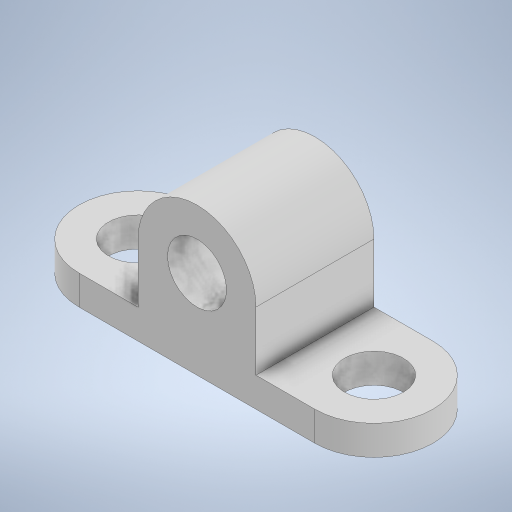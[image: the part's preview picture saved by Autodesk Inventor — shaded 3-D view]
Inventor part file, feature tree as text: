
AUTODESK INVENTOR PART (.ipt)
format: ipt  version: 2024 (Build 280153000, 153)  size: 287,744 bytes
history: native  units: mm
features: extrude x9, sketch x9
ambient origin geometry x8: Origin, YZ Plane, XZ Plane, XY Plane, X Axis, Y Axis, Z Axis, Center Point
bodies: Body1 (feature_tree)
feature tree (18):
  extrude  "Extrusión2"  Depth=40.0mm
  extrude  "Extrusión3"  Depth=40.0mm TaperAngle=0.0deg
  extrude  "Extrusión5"  Depth=10.0mm
  extrude  "Extrusión6"  Depth=20.0mm
  extrude  "Extrusión7"  Depth=40.0mm TaperAngle=0.0deg
  extrude  "Extrusión8"  Depth=10.0mm TaperAngle=0.0deg
  extrude  "Extrusión9"  Depth=40.0mm TaperAngle=0.0deg
  extrude  "Extrusión10"  Depth=10.0mm TaperAngle=0.0deg
  extrude  "Extrusión11"  Depth=10.0mm TaperAngle=0.0deg
  sketch  "Boceto2"  dims[d7=40.0mm d8=30.0mm]
  sketch  "Boceto4"  dims[d9=40.0mm d10=0.0mm d12=40.0mm d13=0.0mm]
  sketch  "Boceto6"  dims[d17=20.0mm d18=10.0mm]
  sketch  "Boceto7"  dims[d19=40.0mm d20=0.0mm d21=20.0mm]
  sketch  "Boceto8"  dims[d22=10.0mm d23=40.0mm d24=0.0mm]
  sketch  "Boceto9"  dims[d26=10.0mm d27=0.0mm d29=10.0mm d30=0.0mm]
  sketch  "Boceto10"  dims[d31=20.0mm d32=40.0mm d33=0.0mm]
  sketch  "Boceto11"  dims[d34=20.0mm d35=10.0mm d36=0.0mm]
  sketch  "Boceto12"  dims[d37=20.0mm d38=10.0mm d39=0.0mm d14=0.5mm d15=0.872665mm d16=0.5mm d28=0.5mm d40=0.5mm d41=0.872665mm d42=0.5mm d43=0.872665mm]
